# Revit family: BARPA_Crux1_LOD5
name_source: partatom
category: Electrical Equipment
revit_build: Autodesk Revit 2016 (Build: 20170117_1200(x64)
units: mm (PartAtom-declared; Revit-internal decimal feet)

## family parameters
Always vertical = Yes
Cut with Voids When Loaded = No
Part Type = Other Panel
Room Calculation Point = No
Round Connector Dimension = Use Diameter
Shared = No
Work Plane-Based = No

## types (12) — shared parameters
BARPA_Color = Black (RAL9004)
BARPA_Datasheet = https://www.barpa.eu
BARPA_Declaration of Conformity = https://www.barpa.eu
BARPA_Description = Crux 1 is the wall cabinet of the barpa range of cabinets. It’s available in a range of heights and depths and accommodates a load of up to 60 kg.
BARPA_Earth Connection = Yes
BARPA_Instructions Manual = https://www.barpa.eu
BARPA_Instructions Video = https://www.youtube.com
BARPA_Loading Capacity = 60.00 kg
BARPA_Material = SPCC Cold Rolled Steel; Mounting profile: 1.2mm; Others 1.0mm
BARPA_Standard = ANSI/EIA RS-310-D; IEC60297-2; DIN41494 Part 1 and 7
BARPA_Width = 570 mm  [stored 1.87008 ft]
IfcExportAs = IfcBuildingElementProxy
IfcExportType = DATACABINET
Manufacturer = BARPA

## per-type parameters (varying)
| type | BARPA_EAN Code | BARPA_Height | BARPA_Length | Description | Model |
| Crux 1 - 6U 570x450 | 5608445006073 | 370 mm  [stored 1.21391 ft] | 450 mm  [stored 1.47638 ft] | Rack Crux 1 - 6U 570x450mm | 82321060604 |
| Crux 1 - 6U 570x600 | 5608445006134 | 370 mm  [stored 1.21391 ft] | 600 mm | Rack Crux 1 - 6U 570x600mm | 82321060606 |
| Crux 1 - 9U 570x450 | 5608445006080 | 500 mm  [stored 1.64042 ft] | 450 mm  [stored 1.47638 ft] | Rack Crux 1 - 9U 570x450mm | 82321090604 |
| Crux 1 - 9U 570x600 | 5608445006141 | 500 mm  [stored 1.64042 ft] | 600 mm | Rack Crux 1 - 9U 570x600mm | 82321090606 |
| Crux 1 - 12U 570x450 | 5608445006097 | 635 mm | 450 mm  [stored 1.47638 ft] | Rack Crux 1 - 12U 570x450mm | 82321120604 |
| Crux 1 - 12U 570x600 | 5608445006158 | 635 mm | 600 mm | Rack Crux 1 - 12U 570x600mm | 82321120606 |
| Crux 1 - 15U 570x450 | 5608445006103 | 770 mm  [stored 2.52625 ft] | 450 mm  [stored 1.47638 ft] | Rack Crux 1 - 15U 570x450mm | 82321150604 |
| Crux 1 - 15U 570x600 | 5608445006165 | 770 mm  [stored 2.52625 ft] | 600 mm | Rack Crux 1 - 15U 570x600mm | 82321150606 |
| Crux 1 - 18U 570x450 | 5608445006110 | 900 mm  [stored 2.95276 ft] | 450 mm  [stored 1.47638 ft] | Rack Crux 1 - 18U 570x450mm | 82321180604 |
| Crux 1 - 18U 570x600 | 5608445006172 | 900 mm  [stored 2.95276 ft] | 600 mm | Rack Crux 1 - 18U 570x600mm | 82321180606 |
| Crux 1 - 22U 570x450 | 5608445006127 | 1080 mm  [stored 3.54331 ft] | 450 mm  [stored 1.47638 ft] | Rack Crux 1 - 22U 570x450mm | 82321220604 |
| Crux 1 - 22U 570x600 | 5608445006189 | 1080 mm  [stored 3.54331 ft] | 600 mm | Rack Crux 1 - 22U 570x600mm | 82321220606 |

note: [stored X ft] marks values corroborated as IEEE doubles in the binary element streams (Revit-internal decimal feet)

## geometry (parser evidence)
native form markers: Sweep x9
no freeform markers — native parametric forms only
